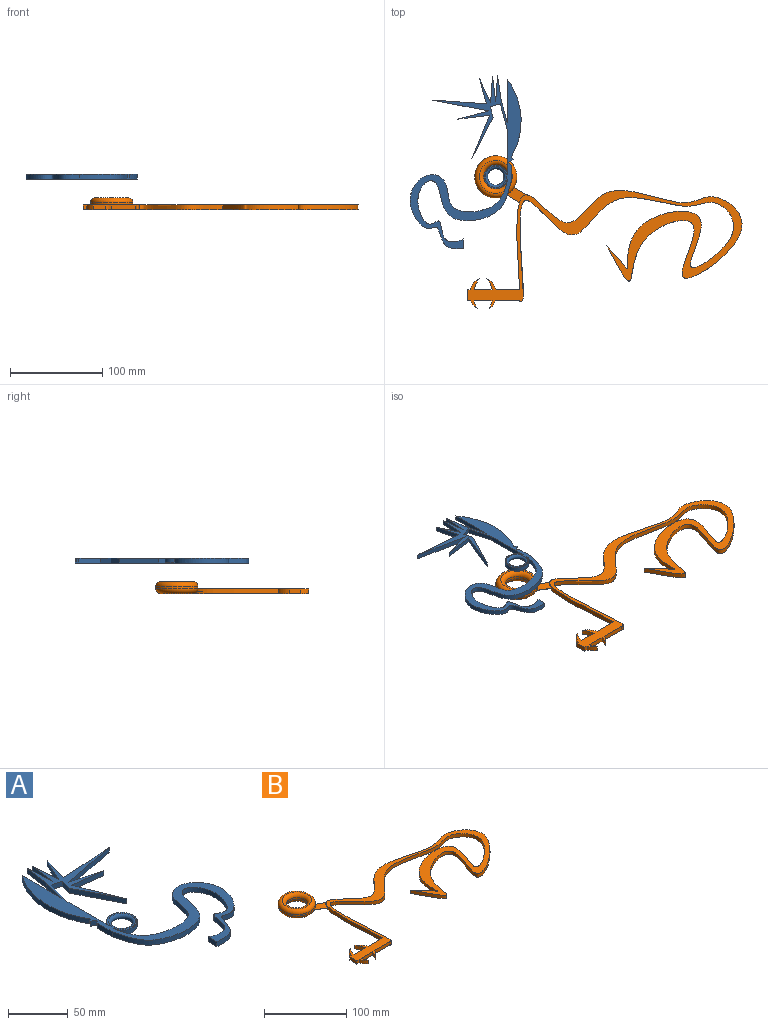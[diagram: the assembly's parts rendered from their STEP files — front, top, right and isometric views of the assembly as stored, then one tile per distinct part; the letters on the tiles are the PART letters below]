
ASSEMBLY  parts=2 mates=1
PART A: 33 faces, bbox 122.2x189.3x5.1 mm
  f0: cylinder r=12.92mm len=25.84mm, axis (0,0,-1), area 338.8mm2, adj f1,f27,f30,f31
  f1: plane 49.08x5.08mm, normal (1,0,0), area 243.8mm2, adj f0,f2,f28,f29,f30,f31
  f2: plane 27.71x7.5mm, normal (0.97,-0.26,0), area 145.9mm2, adj f1,f3,f28,f29
  f3: plane 10.95x5.08mm, normal (-0.26,-0.97,0), area 57.6mm2, adj f2,f4,f28,f29
  f4: plane 11.58x5.08mm, normal (-0.97,0.26,0), area 60.9mm2, adj f3,f5,f28,f29
  f5: plane 44.67x22.99mm, normal (-0.89,-0.46,0), area 255.2mm2, adj f4,f6,f28,f29
  f6: plane 46.85x19.04mm, normal (0.93,0.38,0), area 256.9mm2, adj f5,f7,f28,f29
  f7: plane 34.21x5.08mm, normal (-0.12,-0.99,0), area 175.1mm2, adj f6,f8,f28,f29
  f8: plane 32.95x8.92mm, normal (0.26,0.97,0), area 173.4mm2, adj f7,f9,f28,f29
  f9: plane 60.44x11.81mm, normal (0.19,-0.98,0), area 312.9mm2, adj f8,f10,f28,f29
  f10: plane 58.36x5.08mm, normal (-0.07,1,0), area 297.2mm2, adj f9,f11,f28,f29
  f11: plane 27.03x7.31mm, normal (0.97,-0.26,0), area 142.3mm2, adj f10,f12,f28,f29
  f12: plane 25.78x11.93mm, normal (-0.91,0.42,0), area 144.3mm2, adj f11,f13,f28,f29
  f13: plane 28.92x5.08mm, normal (1,0.07,0), area 147.3mm2, adj f12,f14,f28,f29
  f14: plane 27.44x5.08mm, normal (-0.99,0.12,0), area 140.5mm2, adj f13,f15,f28,f29
  f15: plane 28.31x5.08mm, normal (1,0.07,0), area 144.2mm2, adj f14,f16,f28,f29
  f16: plane 26.71x5.08mm, normal (-0.99,0.15,0), area 137.2mm2, adj f15,f17,f28,f29
  f17: plane 24.41x6.61mm, normal (-0.97,0.26,0), area 128.5mm2, adj f16,f18,f28,f29
  f18: plane 46.94x5.08mm, normal (1,0,0), area 238.5mm2, adj f17,f19,f28,f29
  f19: cylinder r=76.05mm len=84.61mm, axis (0,0,-1), area 456.4mm2, adj f18,f20,f28,f29
  f20: plane 5.08x2.87mm, normal (-0.81,0.58,0), area 17.9mm2, adj f19,f21,f28,f29
  f21: plane 5.08x4.38mm, normal (-0.58,-0.81,0), area 27.3mm2, adj f20,f22,f28,f29
  f22: plane 5.08x3.29mm, normal (-0.81,0.58,0), area 20.5mm2, adj f21,f23,f28,f29
  f23: plane 17.39x5.08mm, normal (-1,0,0), area 88.3mm2, adj f22,f24,f28,f29
  f24: extruded ~100.92x66.23mm, area 1258.7mm2, adj f23,f25,f28,f29
  f25: plane 10.39x5.08mm, normal (-1,0,0), area 52.8mm2, adj f24,f26,f28,f29
  f26: extruded ~105.31x80.15mm, area 1288.7mm2, adj f25,f27,f28,f29
  f27: plane 5.08x2.8mm, normal (1,0,0), area 8.7mm2, adj f0,f26,f28,f29,f30,f31
  f28: plane 189.31x122.17mm, normal (0,0,1), area 3707.4mm2, adj f1,f2,f3,f4,f5,f6,f7,f8
  f29: plane 189.31x122.17mm, normal (0,0,-1), area 3707.4mm2, adj f1,f2,f3,f4,f5,f6,f7,f8
  f30: torus R=12.67mm, axis (0,0,1), area 29.6mm2, adj f0,f1,f27,f29
  f31: torus R=12.67mm, axis (0,0,1), area 29.6mm2, adj f0,f1,f27,f28
  f32: torus R=11.43mm, axis (0,0,1), area 492mm2, adj f28,f29
PART B: 29 faces, bbox 303.2x167.7x12.7 mm
  f0: extruded ~232.04x111.51mm, area 3343.7mm2, adj f1,f16,f17,f18
  f1: extruded ~242.29x107.75mm, area 3515.2mm2, adj f0,f2,f17,f18,f19,f20,f21,f23
  f2: plane 25.39x5.08mm, normal (0,1,0), area 129mm2, adj f1,f3,f17,f18
  f3: cylinder r=19.26mm len=12.67mm, axis (0,0,-1), area 86mm2, adj f2,f4,f17,f18
  f4: cylinder r=29.95mm len=12.67mm, axis (0,0,-1), area 71.7mm2, adj f3,f5,f17,f18
  f5: plane 19.33x5.08mm, normal (0,1,0), area 98.2mm2, adj f4,f6,f17,f18
  f6: cylinder r=29.95mm len=12.67mm, axis (0,0,-1), area 71.7mm2, adj f5,f7,f17,f18
  f7: cylinder r=19.26mm len=12.67mm, axis (0,0,-1), area 86mm2, adj f6,f8,f17,f18
  f8: plane 5.08x2.92mm, normal (0,1,0), area 14.8mm2, adj f7,f9,f17,f18
  f9: plane 11.95x5.08mm, normal (-1,0,0), area 60.7mm2, adj f8,f10,f17,f18
  f10: plane 5.08x3.74mm, normal (0,-1,0), area 19mm2, adj f9,f11,f17,f18
  f11: cylinder r=19.26mm len=8.55mm, axis (0,0,-1), area 56.3mm2, adj f10,f12,f17,f18
  f12: cylinder r=29.95mm len=8.55mm, axis (0,0,-1), area 46.5mm2, adj f11,f13,f17,f18
  f13: plane 19.32x5.08mm, normal (0,-1,0), area 98.1mm2, adj f12,f14,f17,f18
  f14: cylinder r=29.95mm len=8.55mm, axis (0,0,-1), area 46.5mm2, adj f13,f15,f17,f18
  f15: cylinder r=19.26mm len=8.55mm, axis (0,0,-1), area 56.3mm2, adj f14,f16,f17,f18
  f16: plane 26.21x5.08mm, normal (0,-1,0), area 133.2mm2, adj f0,f15,f17,f18
  f17: plane 303.2x134.02mm, normal (0,0,1), area 5819.5mm2, adj f0,f1,f2,f3,f4,f5,f6,f7
  f18: plane 303.2x134.02mm, normal (0,0,-1), area 5819.5mm2, adj f0,f1,f2,f3,f4,f5,f6,f7
  f19: plane 14.47x9.13mm, normal (-0.53,-0.85,0), area 4.3mm2, adj f1,f21,f23,f27
  f20: plane 14.87x8.53mm, normal (0.5,0.87,0), area 4.3mm2, adj f1,f21,f23,f27
  f21: plane 23.15x17.55mm, normal (0,0,1), area 168.9mm2, adj f1,f19,f20,f27
  f22: cylinder r=22.82mm len=45.63mm, axis (0,0,-1), area 364.2mm2, adj f27,f28
  f23: plane 23.3x17.63mm, normal (0,0,-1), area 170.7mm2, adj f1,f19,f20,f27
  f24: cylinder r=12.7mm len=25.4mm, axis (0,0,-1), area 202.7mm2, adj f25,f26
  f25: torus R=17.78mm, axis (0,0,1), area 729.3mm2, adj f24,f28
  f26: torus R=17.78mm, axis (0,0,1), area 729.3mm2, adj f24,f27
  f27: torus R=17.74mm, axis (0,0,-1), area 1043.1mm2, adj f19,f20,f21,f22,f23,f26
  f28: torus R=17.74mm, axis (0,0,1), area 1046.5mm2, adj f22,f25
PLACE A rot(axis=(0,1,0),180deg) t=(-132.06,120.72,-15.53)mm
PLACE B t=(23.75,20.78,-53.63)mm
MATE revolute A.f0 <-> B.f22  axis (0,0,-1) through (-96.8,66.82,-20.61)mm
